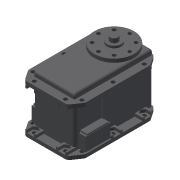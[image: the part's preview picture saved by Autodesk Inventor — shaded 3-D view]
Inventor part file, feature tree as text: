
AUTODESK INVENTOR PART (.ipt)
format: ipt  version: 2020 (Build 240168000, 168)  size: 578,560 bytes
history: native  units: mm
features: other x5, extrude x3, sketch x3, projected_geometry x2
ambient origin geometry x8: Origin, YZ Plane, XZ Plane, XY Plane, X Axis, Y Axis, Z Axis, Center Point
bodies: Body1 (feature_tree)
feature tree (13):
  other  "솔리드1"
  other  "기준1"
  other  "작업 평면1"
  other  "작업 평면2"
  other  "작업 평면3"
  extrude  "돌출1"  [1 undecoded]
  extrude  "돌출2"  [1 undecoded]
  extrude  "돌출3"  Depth=2.5mm
  sketch  "스케치1"
  sketch  "스케치2"
  projected_geometry  "투영된 루프1"
  sketch  "스케치3"
  projected_geometry  "투영된 루프2"
note: 2 required parameter values undecoded (feature->parameter linkage not recoverable at this tier; creation-order binding heuristic only, values carry confidence <= 0.55)
